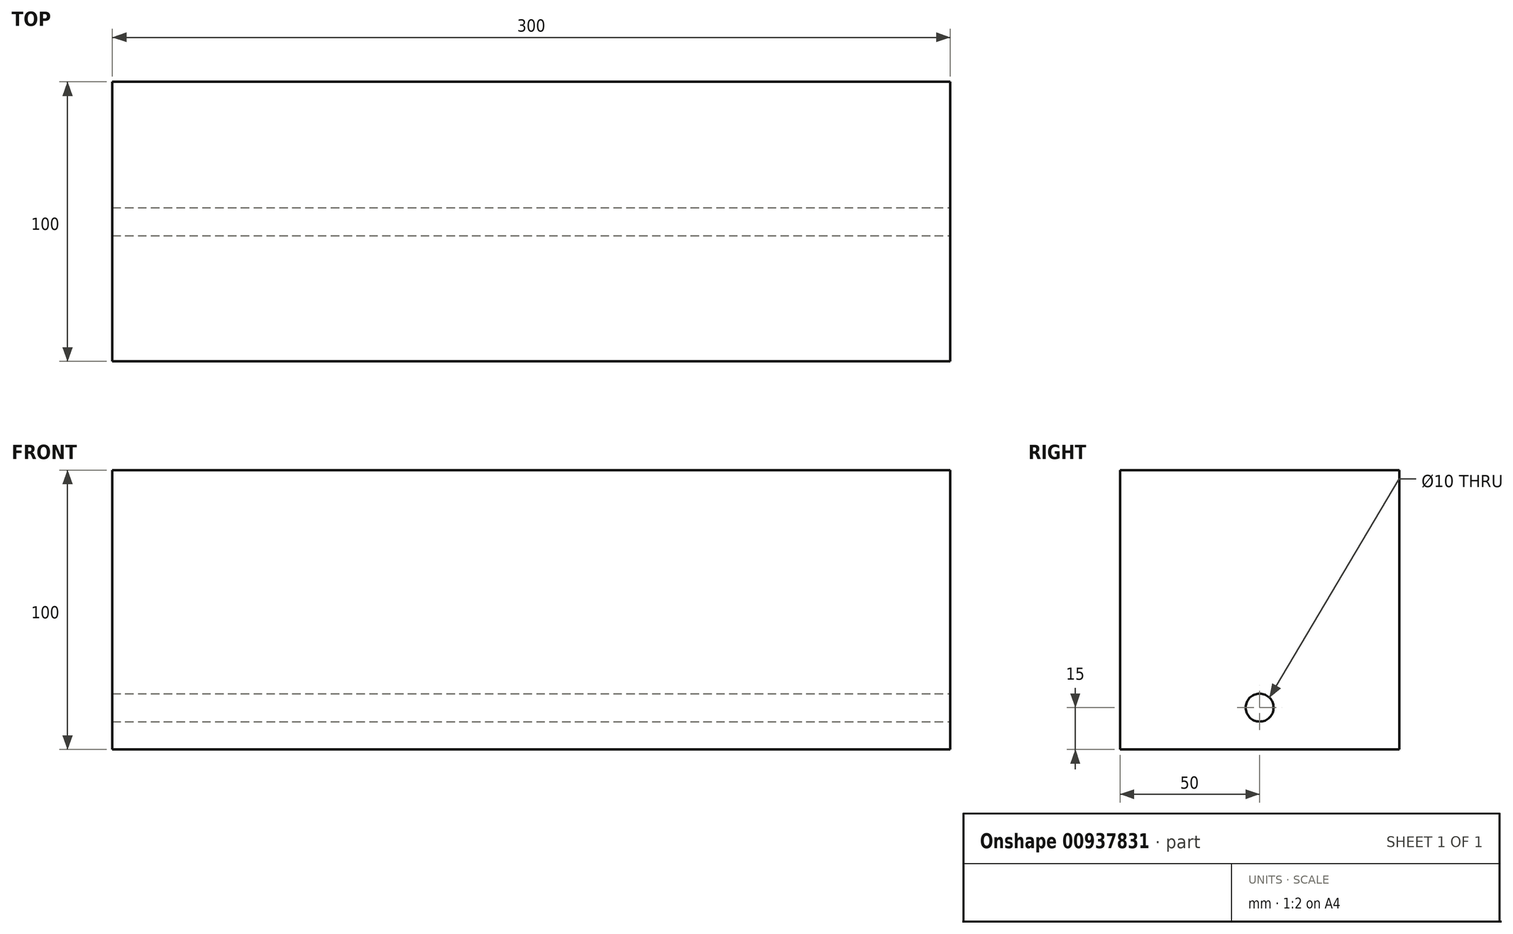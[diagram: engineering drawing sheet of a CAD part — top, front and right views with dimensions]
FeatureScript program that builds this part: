
annotation { "Feature Type Name" : "Feature", "Feature Type Description" : "" }
export const myFeature = defineFeature(function(context is Context, id is Id, definition is map)
    precondition{}
    {
        {
            var Q0;
            Q0=qCreatedBy(makeId("Front.planeOp"),FACE);
            var sketch = newSketch(context, id + "F0", { "sketchPlane" : qUnion([Q0])});
            skLineSegment(sketch, "E0.bottom", {"start": v(-150, 50) * mm, "end": v(150, 50) * mm});
            skLineSegment(sketch, "E0.top", {"start": v(-150, -50) * mm, "end": v(150, -50) * mm});
            skLineSegment(sketch, "E0.left", {"start": v(-150, 50) * mm, "end": v(-150, -50) * mm});
            skLineSegment(sketch, "E0.right", {"start": v(150, 50) * mm, "end": v(150, -50) * mm});
            skPoint(sketch, "E0.middle", {"position": v(0, 0) * mm});
            skSolve(sketch);
        }
        {
            var Q0;
            Q0=makeQuery(id+"F0.imprint","IMPRINT",FACE,{"disambiguationData":[TD([[makeQuery(id+"F0.imprint","IMPRINT",EDGE,{"derivedFrom":sQuery(id+"F0.wireOp",EDGE,"E0.bottom")}),-1.0]])]});
            extrude(context, id + "F1", {"entities" : qUnion([Q0]), "depth" : 100 * mm, "offsetDistance" : 25 * mm});
        }
        {
            var Q0;
            Q0=makeQuery(id+"F1.opExtrude","SWEPT_FACE",FACE,{"disambiguationData":[OSD([sQuery(id+"F0.wireOp",EDGE,"E0.right")])]});
            var sketch = newSketch(context, id + "F2", { "sketchPlane" : qUnion([Q0])});
            skCircle(sketch, "E1", {"center": v(-50, -35) * mm, "radius": 5 * mm});
            skSolve(sketch);
        }
        {
            var Q0;
            Q0=qSketchRegion(id+"F2",true);
            extrude(context, id + "F3", {"entities" : qUnion([Q0]), "operationType" : NewBodyOperationType.REMOVE, "oppositeDirection" : true, "depth" : 300 * mm, "offsetDistance" : 25 * mm});
        }
    });
